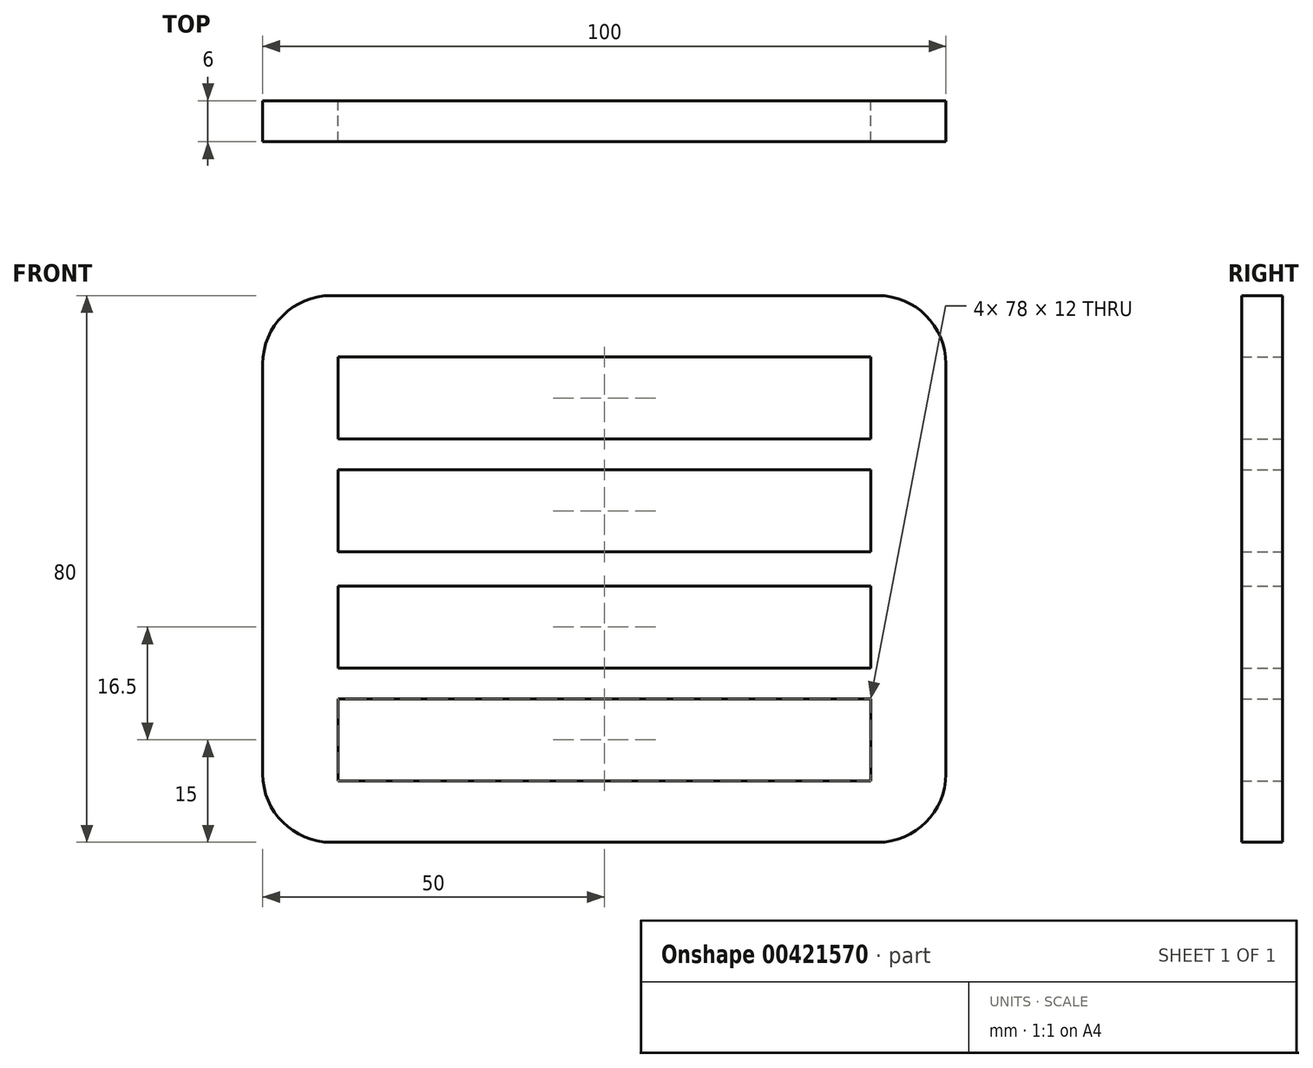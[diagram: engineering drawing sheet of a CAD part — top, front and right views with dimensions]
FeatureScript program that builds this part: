
annotation { "Feature Type Name" : "Feature", "Feature Type Description" : "" }
export const myFeature = defineFeature(function(context is Context, id is Id, definition is map)
    precondition{}
    {
        {
            var Q0;
            Q0=qCreatedBy(makeId("Front.planeOp"),FACE);
            var sketch = newSketch(context, id + "F0", { "sketchPlane" : qUnion([Q0])});
            skLineSegment(sketch, "E0.bottom", {"start": v(-50, 40) * mm, "end": v(50, 40) * mm});
            skLineSegment(sketch, "E0.top", {"start": v(-50, -40) * mm, "end": v(50, -40) * mm});
            skLineSegment(sketch, "E0.left", {"start": v(-50, 40) * mm, "end": v(-50, -40) * mm});
            skLineSegment(sketch, "E0.right", {"start": v(50, 40) * mm, "end": v(50, -40) * mm});
            skLineSegment(sketch, "E1", {"start": v(-39, 31) * mm, "end": v(-39, 19) * mm});
            skLineSegment(sketch, "E2", {"start": v(-39, 19) * mm, "end": v(39, 19) * mm});
            skLineSegment(sketch, "E3", {"start": v(39, 19) * mm, "end": v(39, 31) * mm});
            skLineSegment(sketch, "E4", {"start": v(39, 31) * mm, "end": v(-39, 31) * mm});
            skLineSegment(sketch, "E5", {"start": v(-39, 14.5) * mm, "end": v(-39, 2.5) * mm});
            skLineSegment(sketch, "E6", {"start": v(-39, 2.5) * mm, "end": v(39, 2.5) * mm});
            skLineSegment(sketch, "E7", {"start": v(39, 2.5) * mm, "end": v(39, 14.5) * mm});
            skLineSegment(sketch, "E8", {"start": v(39, 14.5) * mm, "end": v(-39, 14.5) * mm});
            skLineSegment(sketch, "E9.MirrorCS", {"start": v(-39, -2.5) * mm, "end": v(39, -2.5) * mm});
            skLineSegment(sketch, "E10.MirrorCS", {"start": v(39, -14.5) * mm, "end": v(-39, -14.5) * mm});
            skLineSegment(sketch, "E11.MirrorCS", {"start": v(-39, -14.5) * mm, "end": v(-39, -2.5) * mm});
            skLineSegment(sketch, "E12.MirrorCS", {"start": v(39, -2.5) * mm, "end": v(39, -14.5) * mm});
            skLineSegment(sketch, "E13.MirrorCS", {"start": v(-39, -19) * mm, "end": v(39, -19) * mm});
            skLineSegment(sketch, "E14.MirrorCS", {"start": v(39, -31) * mm, "end": v(-39, -31) * mm});
            skLineSegment(sketch, "E15.MirrorCS", {"start": v(-39, -31) * mm, "end": v(-39, -19) * mm});
            skLineSegment(sketch, "E16.MirrorCS", {"start": v(39, -19) * mm, "end": v(39, -31) * mm});
            skSolve(sketch);
        }
        {
            var Q0;
            Q0=qSketchRegion(id+"F0",true);
            extrude(context, id + "F1", {"entities" : qUnion([Q0]), "depth" : 6 * mm, "offsetDistance" : 25 * mm});
        }
        {
            var Q0;
            Q0=makeQuery(id+"F1.opExtrude","SWEPT_EDGE",EDGE,{"disambiguationData":[OSD([sQuery(id+"F0.wireOp",EDGE,"E0.bottom"),sQuery(id+"F0.wireOp",EDGE,"E0.right")])]});
            var Q1;
            Q1=makeQuery(id+"F1.opExtrude","SWEPT_EDGE",EDGE,{"disambiguationData":[OSD([sQuery(id+"F0.wireOp",EDGE,"E0.top"),sQuery(id+"F0.wireOp",EDGE,"E0.left")])]});
            var Q2;
            Q2=makeQuery(id+"F1.opExtrude","SWEPT_EDGE",EDGE,{"disambiguationData":[OSD([sQuery(id+"F0.wireOp",EDGE,"E0.bottom"),sQuery(id+"F0.wireOp",EDGE,"E0.left")])]});
            var Q3;
            Q3=makeQuery(id+"F1.opExtrude","SWEPT_EDGE",EDGE,{"disambiguationData":[OSD([sQuery(id+"F0.wireOp",EDGE,"E0.top"),sQuery(id+"F0.wireOp",EDGE,"E0.right")])]});
            fillet(context, id + "F2", {"entities" : qUnion([Q0, Q1, Q2, Q3]), "radius" : 10 * mm, "tangentPropagation" : true, "allowEdgeOverflow" : false});
        }
    });
